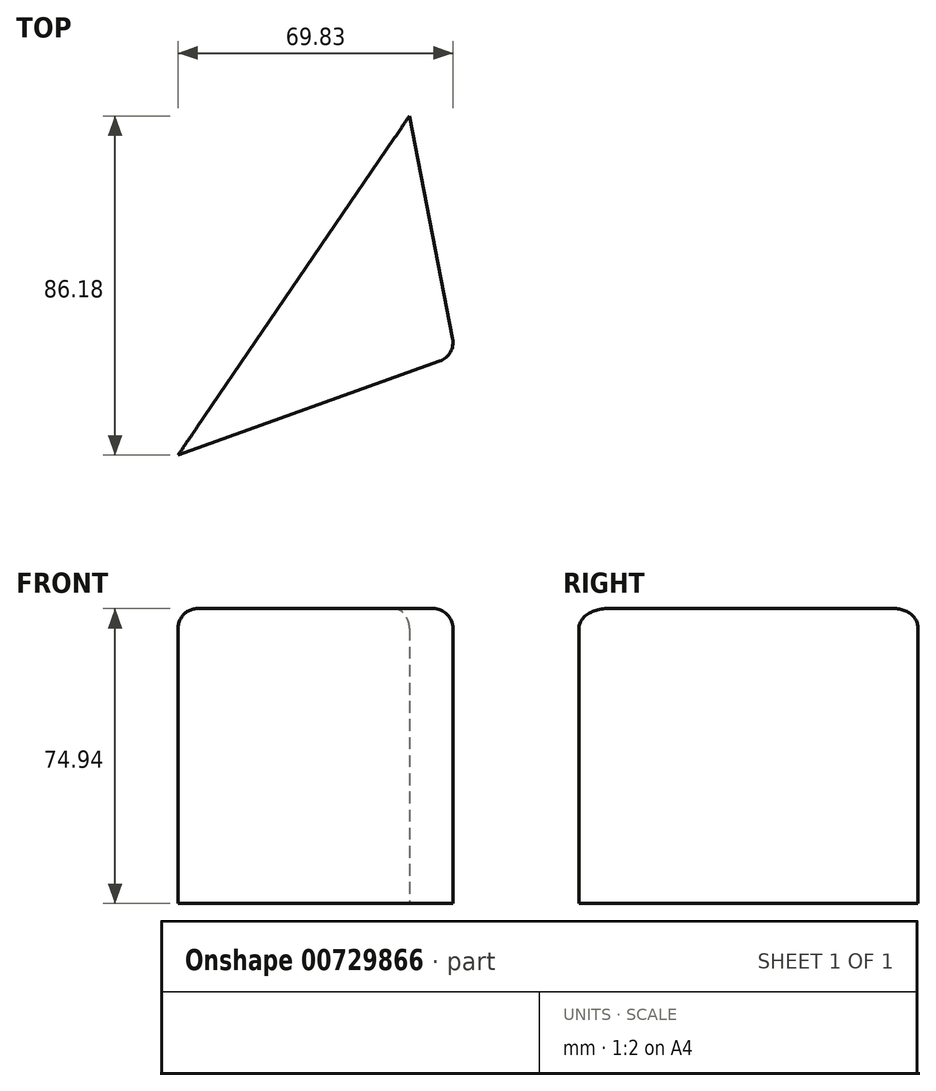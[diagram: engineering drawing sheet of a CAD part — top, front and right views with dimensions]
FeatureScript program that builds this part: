
annotation { "Feature Type Name" : "Feature", "Feature Type Description" : "" }
export const myFeature = defineFeature(function(context is Context, id is Id, definition is map)
    precondition{}
    {
        {
            var Q0;
            Q0=qCreatedBy(makeId("Top.planeOp"),FACE);
            var sketch = newSketch(context, id + "F0", { "sketchPlane" : qUnion([Q0])});
            skLineSegment(sketch, "E0", {"start": v(26.37, 35.65) * mm, "end": v(-32.41, -50.53) * mm});
            skLineSegment(sketch, "E1", {"start": v(-32.41, -50.53) * mm, "end": v(38.16, -25.2) * mm});
            skLineSegment(sketch, "E2", {"start": v(38.16, -25.2) * mm, "end": v(26.37, 35.65) * mm});
            skSolve(sketch);
        }
        {
            var Q0;
            Q0=makeQuery(id+"F0.imprint","IMPRINT",FACE,{"disambiguationData":[TD([[makeQuery(id+"F0.imprint","IMPRINT",EDGE,{"derivedFrom":sQuery(id+"F0.wireOp",EDGE,"E0")}),1.0]])]});
            extrude(context, id + "F1", {"entities" : qUnion([Q0]), "depth" : 74.94 * mm, "offsetDistance" : 25.4 * mm});
        }
        {
            var Q0;
            Q0=makeQuery(id+"F1.opExtrude","CAP_EDGE",EDGE,{"disambiguationData":[OSD([sQuery(id+"F0.wireOp",EDGE,"E1")])],"isStart":false});
            var Q1;
            Q1=makeQuery(id+"F1.opExtrude","CAP_EDGE",EDGE,{"disambiguationData":[OSD([sQuery(id+"F0.wireOp",EDGE,"E2")])],"isStart":false});
            var Q2;
            Q2=makeQuery(id+"F1.opExtrude","SWEPT_EDGE",EDGE,{"disambiguationData":[OSD([sQuery(id+"F0.wireOp",EDGE,"E1"),sQuery(id+"F0.wireOp",EDGE,"E2")])]});
            fillet(context, id + "F2", {"entities" : qUnion([Q0, Q1, Q2]), "radius" : 5.08 * mm, "tangentPropagation" : true, "allowEdgeOverflow" : false});
        }
    });
